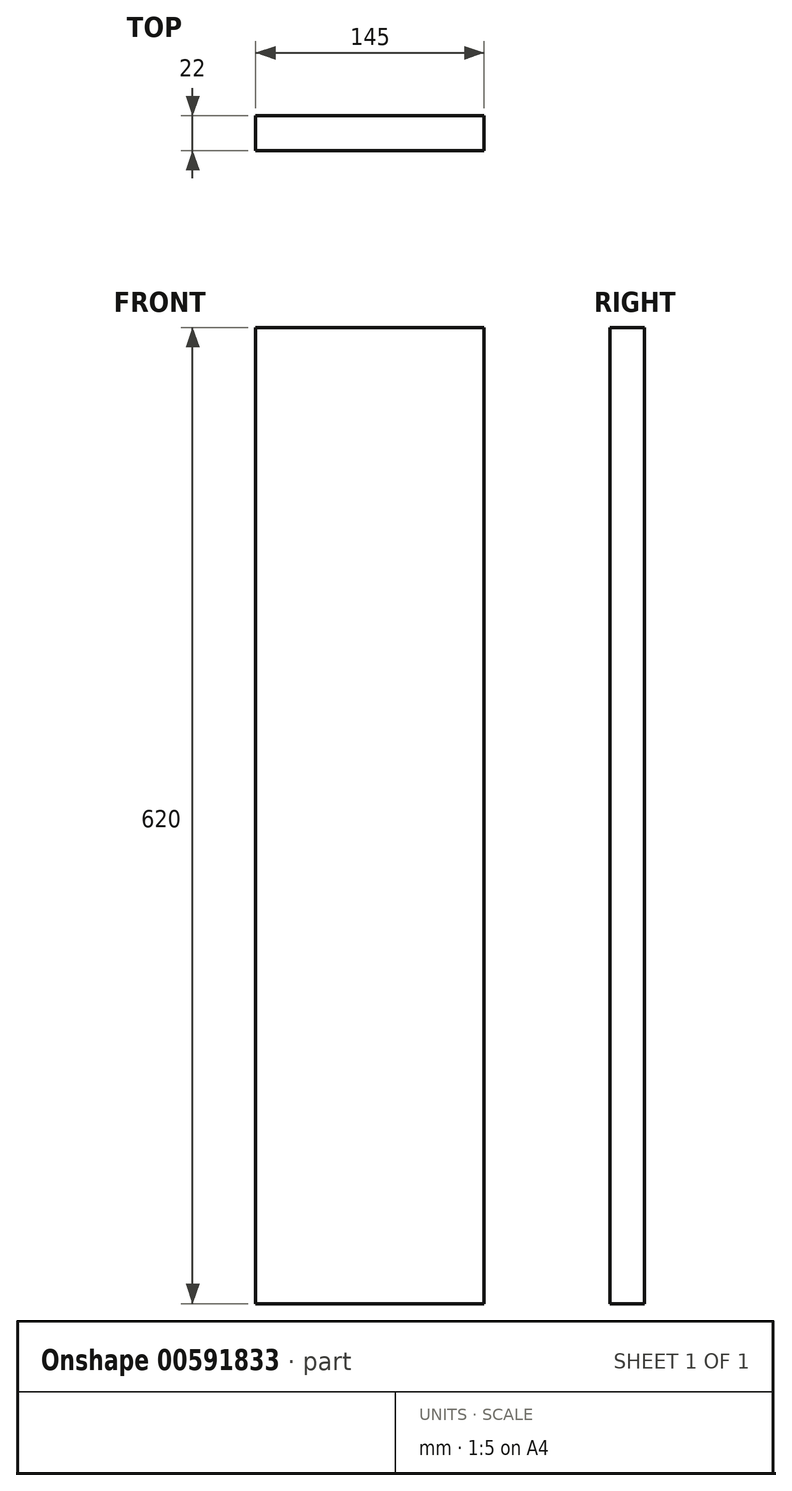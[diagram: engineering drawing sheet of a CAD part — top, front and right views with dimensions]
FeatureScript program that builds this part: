
annotation { "Feature Type Name" : "Feature", "Feature Type Description" : "" }
export const myFeature = defineFeature(function(context is Context, id is Id, definition is map)
    precondition{}
    {
        {
            var Q0;
            Q0=qCreatedBy(makeId("Top.planeOp"),FACE);
            var sketch = newSketch(context, id + "F0", { "sketchPlane" : qUnion([Q0])});
            skLineSegment(sketch, "E0.bottom", {"start": v(0, 0) * mm, "end": v(145, 0) * mm});
            skLineSegment(sketch, "E0.top", {"start": v(0, 22) * mm, "end": v(145, 22) * mm});
            skLineSegment(sketch, "E0.left", {"start": v(0, 0) * mm, "end": v(0, 22) * mm});
            skLineSegment(sketch, "E0.right", {"start": v(145, 0) * mm, "end": v(145, 22) * mm});
            skSolve(sketch);
        }
        {
            var Q0;
            Q0=makeQuery(id+"F0.imprint","IMPRINT",FACE,{"disambiguationData":[TD([[makeQuery(id+"F0.imprint","IMPRINT",EDGE,{"derivedFrom":sQuery(id+"F0.wireOp",EDGE,"E0.bottom")}),1.0]])]});
            extrude(context, id + "F1", {"entities" : qUnion([Q0]), "depth" : 620 * mm, "offsetDistance" : 25 * mm});
        }
    });
